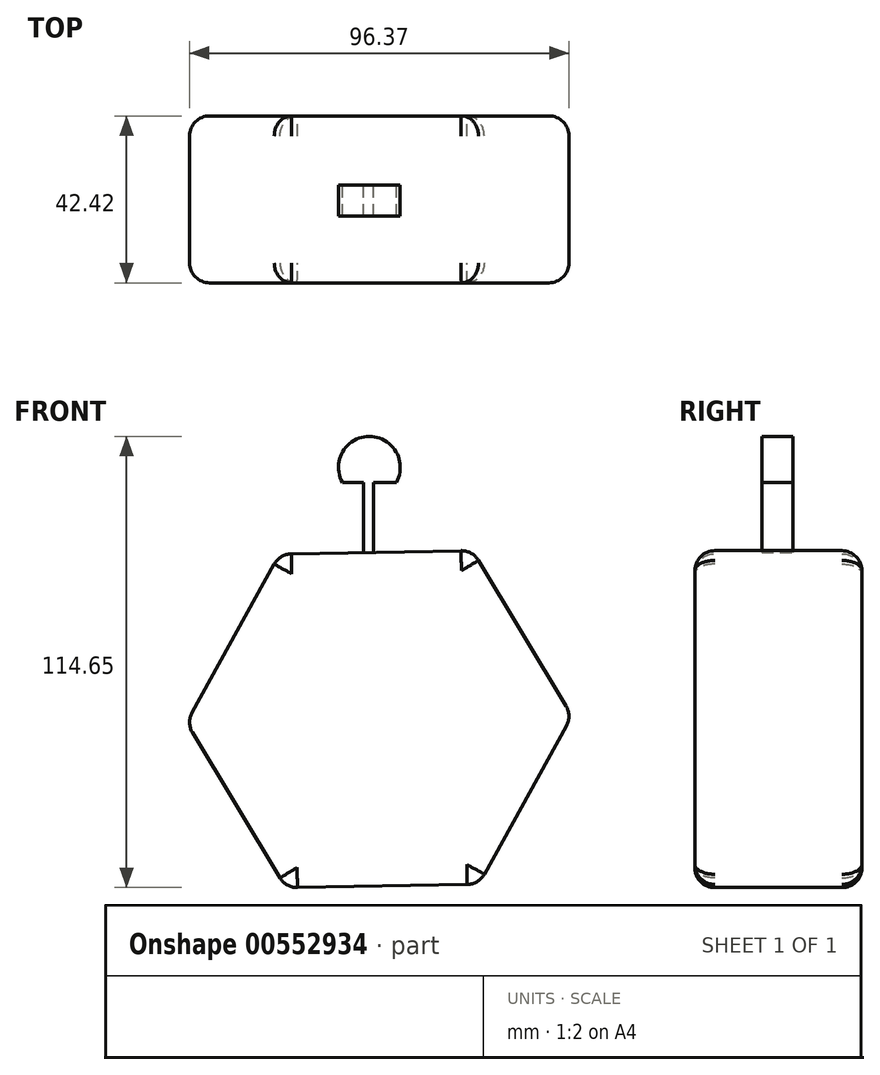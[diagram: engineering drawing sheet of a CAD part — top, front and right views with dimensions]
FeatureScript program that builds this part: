
annotation { "Feature Type Name" : "Feature", "Feature Type Description" : "" }
export const myFeature = defineFeature(function(context is Context, id is Id, definition is map)
    precondition{}
    {
        {
            var Q0;
            Q0=qCreatedBy(makeId("Front.planeOp"),FACE);
            var sketch = newSketch(context, id + "F0", { "sketchPlane" : qUnion([Q0])});
            skLineSegment(sketch, "E0.0", {"start": v(29.51, -30.46) * mm, "end": v(5.8, -73.3) * mm});
            skLineSegment(sketch, "E0.1", {"start": v(5.8, -73.3) * mm, "end": v(-43.17, -74.2) * mm});
            skLineSegment(sketch, "E0.2", {"start": v(-43.17, -74.2) * mm, "end": v(-68.42, -32.23) * mm});
            skLineSegment(sketch, "E0.3", {"start": v(-68.42, -32.23) * mm, "end": v(-44.7, 10.62) * mm});
            skLineSegment(sketch, "E0.4", {"start": v(-44.7, 10.62) * mm, "end": v(4.26, 11.5) * mm});
            skLineSegment(sketch, "E0.5", {"start": v(4.26, 11.5) * mm, "end": v(29.51, -30.46) * mm});
            skPoint(sketch, "E0.0.midPoint", {"position": v(17.65, -51.88) * mm});
            skSolve(sketch);
        }
        {
            var Q0;
            Q0 = qSketchRegion(id + "F0", true);
            extrude(context, id + "F1", {"entities" : qUnion([Q0]), "depth" : 42.42 * mm, "offsetDistance" : 25.4 * mm});
        }
        {
            var Q0;
            Q0=qCreatedBy(makeId("Front.planeOp"),FACE);
            var sketch = newSketch(context, id + "F2", { "sketchPlane" : qUnion([Q0])});
            skLineSegment(sketch, "E1", {"start": v(-23.42, 23.42) * mm, "end": v(-23.42, -51.16) * mm});
            skLineSegment(sketch, "E2", {"start": v(-20.9, 28.82) * mm, "end": v(-20.9, -54.4) * mm});
            skLineSegment(sketch, "E3", {"start": v(-23.42, -51.16) * mm, "end": v(-20.9, -54.4) * mm});
            skLineSegment(sketch, "E4", {"start": v(-23.42, 23.42) * mm, "end": v(-23.42, 28.82) * mm});
            skLineSegment(sketch, "E5", {"start": v(-23.42, 28.82) * mm, "end": v(-20.9, 28.82) * mm});
            skLineSegment(sketch, "E6", {"start": v(-28.82, 28.82) * mm, "end": v(-15.13, 28.82) * mm});
            skArc(sketch, "E7", {"start": v(-15.13, 28.82) * mm, "mid": v(-21.98, 40.5) * mm, "end": v(-28.82, 28.82) * mm});
            skSolve(sketch);
        }
        {
            var Q0;
            Q0 = qSketchRegion(id + "F2", true);
            extrude(context, id + "F3", {"entities" : qUnion([Q0]), "operationType" : NewBodyOperationType.ADD, "depth" : 25.4 * mm, "offsetDistance" : 25.4 * mm, "hasSecondDirection" : true, "secondDirectionOppositeDirection" : false, "secondDirectionDepth" : 17.53 * mm});
        }
        {
            var Q0;
            Q0=makeQuery(id+"F1.opExtrude","SWEPT_FACE",FACE,{"disambiguationData":[OSD([sQuery(id+"F0.wireOp",EDGE,"E0.3")])]});
            var Q1;
            Q1=makeQuery(id+"F1.opExtrude","SWEPT_FACE",FACE,{"disambiguationData":[OSD([sQuery(id+"F0.wireOp",EDGE,"E0.2")])]});
            var Q2;
            Q2=makeQuery(id+"F1.opExtrude","SWEPT_FACE",FACE,{"disambiguationData":[OSD([sQuery(id+"F0.wireOp",EDGE,"E0.5")])]});
            var Q3;
            Q3=makeQuery(id+"F1.opExtrude","SWEPT_FACE",FACE,{"disambiguationData":[OSD([sQuery(id+"F0.wireOp",EDGE,"E0.0")])]});
            fillet(context, id + "F4", {"entities" : qUnion([Q0, Q1, Q2, Q3]), "radius" : 5.08 * mm, "tangentPropagation" : true, "allowEdgeOverflow" : false});
        }
        {
            var Q0;
            Q0=makeQuery(id+"F1.opExtrude","CAP_FACE",FACE,{"disambiguationData":[OSD([sQuery(id+"F0.wireOp",EDGE,"E0.0"),sQuery(id+"F0.wireOp",EDGE,"E0.1"),sQuery(id+"F0.wireOp",EDGE,"E0.2"),sQuery(id+"F0.wireOp",EDGE,"E0.3"),sQuery(id+"F0.wireOp",EDGE,"E0.4"),sQuery(id+"F0.wireOp",EDGE,"E0.5")])],"isStart":false});
            fillet(context, id + "F5", {"entities" : qUnion([Q0]), "radius" : 5.08 * mm, "tangentPropagation" : true, "allowEdgeOverflow" : false});
        }
        {
            var Q0;
            Q0=makeQuery(id+"F1.opExtrude","CAP_FACE",FACE,{"disambiguationData":[OSD([sQuery(id+"F0.wireOp",EDGE,"E0.0"),sQuery(id+"F0.wireOp",EDGE,"E0.1"),sQuery(id+"F0.wireOp",EDGE,"E0.2"),sQuery(id+"F0.wireOp",EDGE,"E0.3"),sQuery(id+"F0.wireOp",EDGE,"E0.4"),sQuery(id+"F0.wireOp",EDGE,"E0.5")])],"isStart":true});
            fillet(context, id + "F6", {"entities" : qUnion([Q0]), "radius" : 5.08 * mm, "tangentPropagation" : true, "allowEdgeOverflow" : false});
        }
    });
